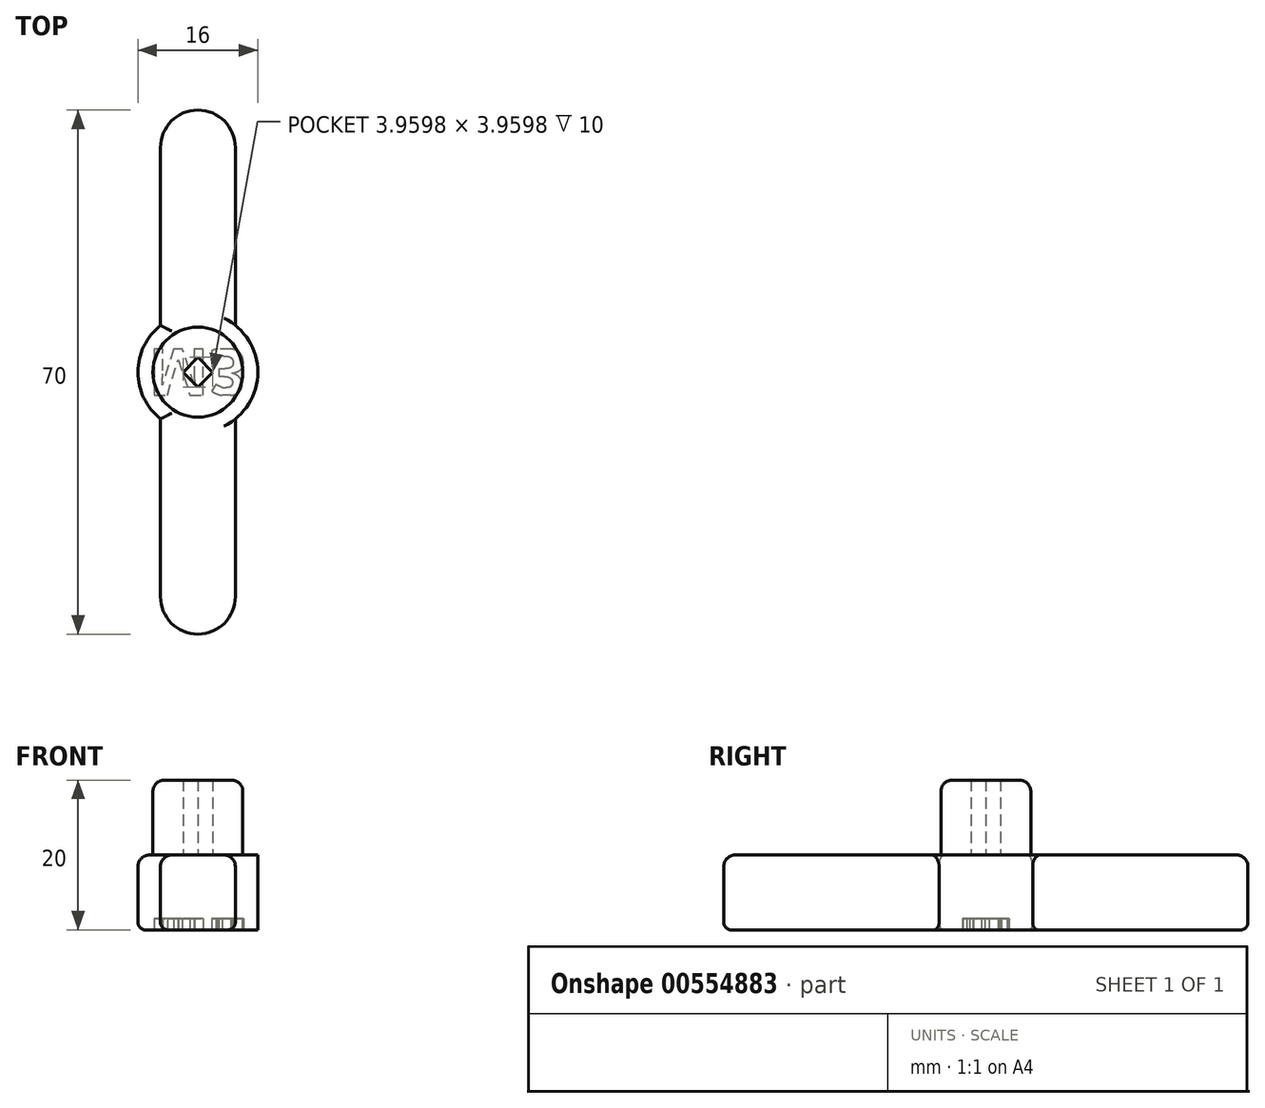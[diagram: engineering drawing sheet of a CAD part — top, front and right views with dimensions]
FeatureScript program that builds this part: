
annotation { "Feature Type Name" : "Feature", "Feature Type Description" : "" }
export const myFeature = defineFeature(function(context is Context, id is Id, definition is map)
    precondition{}
    {
        {
            var Q0;
            Q0=qCreatedBy(makeId("Top.planeOp"),FACE);
            var sketch = newSketch(context, id + "F0", { "sketchPlane" : qUnion([Q0])});
            skLineSegment(sketch, "E0.bottom", {"start": v(5, -30) * mm, "end": v(-5, -30) * mm});
            skLineSegment(sketch, "E0.top", {"start": v(5, 30) * mm, "end": v(-5, 30) * mm});
            skLineSegment(sketch, "E0.left", {"start": v(5, -30) * mm, "end": v(5, 30) * mm});
            skLineSegment(sketch, "E0.right", {"start": v(-5, -30) * mm, "end": v(-5, 30) * mm});
            skPoint(sketch, "E0.middle", {"position": v(0, 0) * mm});
            skArc(sketch, "E1", {"start": v(5, 30) * mm, "mid": v(0, 35) * mm, "end": v(-5, 30) * mm});
            skArc(sketch, "E2", {"start": v(-5, -30) * mm, "mid": v(0, -35) * mm, "end": v(5, -30) * mm});
            skCircle(sketch, "E3", {"center": v(0, 0) * mm, "radius": 8 * mm});
            skCircle(sketch, "E4", {"center": v(0, 0) * mm, "radius": 6 * mm});
            skCircle(sketch, "E5.cCircle", {"center": v(0, 0) * mm, "radius": 2.83 * mm, "construction": true});
            skLineSegment(sketch, "E5.0", {"start": v(0, -2.83) * mm, "end": v(-2.83, 0) * mm});
            skLineSegment(sketch, "E5.1", {"start": v(-2.83, 0) * mm, "end": v(0, 2.83) * mm});
            skLineSegment(sketch, "E5.2", {"start": v(0, 2.83) * mm, "end": v(2.83, 0) * mm});
            skLineSegment(sketch, "E5.3", {"start": v(2.83, 0) * mm, "end": v(0, -2.83) * mm});
            skSolve(sketch);
        }
        {
            var Q0;
            Q0=makeQuery(id+"F0.imprint","IMPRINT",FACE,{"disambiguationData":[TD([[makeQuery(id+"F0.imprint","IMPRINT",EDGE,{"derivedFrom":sQuery(id+"F0.wireOp",EDGE,"E5.0")}),1.0]])]});
            var Q1;
            {var subQ0=sQuery(id+"F0.wireOp",EDGE,"E4");var subQ1=sQuery(id+"F0.wireOp",EDGE,"E0.left");var subQ2=makeQuery(id+"F0.imprint","INTERSECT",VERTEX,{"disambiguationData":[OD(0.0)],"derivedFrom":[subQ1,subQ0]});Q1=makeQuery(id+"F0.imprint","IMPRINT",FACE,{"disambiguationData":[TD([[makeQuery(id+"F0.imprint","IMPRINT",EDGE,{"disambiguationData":[TD([[subQ2,-1.0]])],"derivedFrom":subQ1}),-1.0]])]});}
            var Q2;
            {var subQ0=sQuery(id+"F0.wireOp",EDGE,"E4");var subQ1=sQuery(id+"F0.wireOp",EDGE,"E0.right");var subQ2=makeQuery(id+"F0.imprint","INTERSECT",VERTEX,{"disambiguationData":[OD(0.0)],"derivedFrom":[subQ1,subQ0]});Q2=makeQuery(id+"F0.imprint","IMPRINT",FACE,{"disambiguationData":[TD([[makeQuery(id+"F0.imprint","IMPRINT",EDGE,{"disambiguationData":[TD([[subQ2,-1.0]])],"derivedFrom":subQ1}),1.0]])]});}
            extrude(context, id + "F1", {"entities" : qUnion([Q0, Q1, Q2]), "depth" : 20 * mm, "offsetDistance" : 25 * mm});
        }
        {
            var Q0;
            Q0 = qSketchRegion(id + "F0", true);
            extrude(context, id + "F2", {"entities" : qUnion([Q0]), "operationType" : NewBodyOperationType.ADD, "depth" : 10 * mm, "offsetDistance" : 25 * mm});
        }
        {
            var Q0;
            Q0=qCreatedBy(makeId("Top.planeOp"),FACE);
            var sketch = newSketch(context, id + "F3", { "sketchPlane" : qUnion([Q0])});
            skCircle(sketch, "E6", {"center": v(0, 0) * mm, "radius": 3.52 * mm});
            skSolve(sketch);
        }
        {
            var Q0;
            Q0=makeQuery(id+"F3.imprint","IMPRINT",FACE,{"disambiguationData":[TD([[makeQuery(id+"F3.imprint","IMPRINT",EDGE,{"derivedFrom":sQuery(id+"F3.wireOp",EDGE,"E6")}),1.0]])]});
            extrude(context, id + "F4", {"entities" : qUnion([Q0]), "operationType" : NewBodyOperationType.ADD, "depth" : 10 * mm, "offsetDistance" : 25 * mm});
        }
        {
            var Q0;
            {var subQ0=sQuery(id+"F0.wireOp",EDGE,"E4");Q0=makeQuery(id+"F4.boolean.opBoolean","MERGE",FACE,{"derivedFrom":[makeQuery(id+"F2.boolean.opBoolean","MERGE",FACE,{"derivedFrom":[makeQuery(id+"F1.opExtrude","CAP_FACE",FACE,{"disambiguationData":[OSD([subQ0,sQuery(id+"F0.wireOp",EDGE,"E5.0"),sQuery(id+"F0.wireOp",EDGE,"E5.1"),sQuery(id+"F0.wireOp",EDGE,"E5.2"),sQuery(id+"F0.wireOp",EDGE,"E5.3")])],"isStart":true}),makeQuery(id+"F2.opExtrude","CAP_FACE",FACE,{"disambiguationData":[OSD([sQuery(id+"F0.wireOp",EDGE,"E0.left"),sQuery(id+"F0.wireOp",EDGE,"E0.right"),sQuery(id+"F0.wireOp",EDGE,"E1"),sQuery(id+"F0.wireOp",EDGE,"E2"),sQuery(id+"F0.wireOp",EDGE,"E3"),subQ0])],"isStart":true})]}),makeQuery(id+"F4.opExtrude","CAP_FACE",FACE,{"disambiguationData":[OSD([sQuery(id+"F3.wireOp",EDGE,"E6")])],"isStart":true})]});}
            var sketch = newSketch(context, id + "F5", { "sketchPlane" : qUnion([Q0])});
            skLineSegment(sketch, "E7.bottom", {"start": v(6.64, -3.1) * mm, "end": v(-6.64, -3.1) * mm});
            skLineSegment(sketch, "E7.top", {"start": v(6.64, 3.1) * mm, "end": v(-6.64, 3.1) * mm});
            skLineSegment(sketch, "E7.left", {"start": v(6.64, -3.1) * mm, "end": v(6.64, 3.1) * mm});
            skLineSegment(sketch, "E7.right", {"start": v(-6.64, -3.1) * mm, "end": v(-6.64, 3.1) * mm});
            skPoint(sketch, "E7.middle", {"position": v(0, 0) * mm});
            skText(sketch, "E8", { "text": "M3\n", "fontName": "OpenSans-Bold.ttf"});
            const initialGuessF5  = {"E8": [-0.00664, -0.0031, 1, 0, 0.00621]};
            skSetInitialGuess(sketch, initialGuessF5);
            skSolve(sketch);
        }
        {
            var Q0;
            Q0=makeQuery(id+"F5.imprint","IMPRINT",FACE,{"disambiguationData":[TD([[makeQuery(id+"F5.imprint","IMPRINT",EDGE,{"derivedFrom":sQuery(id+"F5.wireOp",EDGE,"E8.sketch_text.stroke-19")}),-1.0]])]});
            var Q1;
            Q1=makeQuery(id+"F5.imprint","IMPRINT",FACE,{"disambiguationData":[TD([[makeQuery(id+"F5.imprint","IMPRINT",EDGE,{"derivedFrom":sQuery(id+"F5.wireOp",EDGE,"E8.sketch_text.stroke-0")}),-1.0]])]});
            extrude(context, id + "F6", {"entities" : qUnion([Q0, Q1]), "operationType" : NewBodyOperationType.REMOVE, "oppositeDirection" : true, "depth" : 1.5 * mm, "offsetDistance" : 25 * mm});
        }
        {
            var Q0;
            Q0=makeQuery(id+"F1.opExtrude","CAP_EDGE",EDGE,{"disambiguationData":[OSD([sQuery(id+"F0.wireOp",EDGE,"E4")])],"isStart":false});
            fillet(context, id + "F7", {"entities" : qUnion([Q0]), "radius" : 1.5 * mm, "tangentPropagation" : true, "allowEdgeOverflow" : false});
        }
        {
            var Q0;
            Q0=makeQuery(id+"F2.opExtrude","CAP_EDGE",EDGE,{"disambiguationData":[OSD([sQuery(id+"F0.wireOp",EDGE,"E2")])],"isStart":false});
            var Q1;
            {var subQ0=sQuery(id+"F0.wireOp",EDGE,"E0.right");Q1=makeQuery(id+"F2.opExtrude","CAP_EDGE",EDGE,{"disambiguationData":[OSD([subQ0]),TDD([makeQuery(id+"F0.imprint","IMPRINT",EDGE,{"disambiguationData":[TD([[makeQuery(id+"F0.imprint","INTERSECT",VERTEX,{"disambiguationData":[OD(0.0)],"derivedFrom":[subQ0,sQuery(id+"F0.wireOp",EDGE,"E3")]}),1.0]])],"derivedFrom":subQ0})])],"isStart":false});}
            var Q2;
            {var subQ0=sQuery(id+"F0.wireOp",EDGE,"E3");var subQ1=sQuery(id+"F0.wireOp",EDGE,"E0.right");Q2=makeQuery(id+"F2.opExtrude","CAP_EDGE",EDGE,{"disambiguationData":[OSD([subQ0]),TDD([makeQuery(id+"F0.imprint","IMPRINT",EDGE,{"disambiguationData":[TD([[makeQuery(id+"F0.imprint","INTERSECT",VERTEX,{"disambiguationData":[OD(0.0)],"derivedFrom":[subQ1,subQ0]}),1.0]])],"derivedFrom":subQ0})])],"isStart":false});}
            var Q3;
            {var subQ0=sQuery(id+"F0.wireOp",EDGE,"E0.right");Q3=makeQuery(id+"F2.opExtrude","CAP_EDGE",EDGE,{"disambiguationData":[OSD([subQ0]),TDD([makeQuery(id+"F0.imprint","IMPRINT",EDGE,{"disambiguationData":[TD([[makeQuery(id+"F0.imprint","INTERSECT",VERTEX,{"disambiguationData":[OD(1.0)],"derivedFrom":[subQ0,sQuery(id+"F0.wireOp",EDGE,"E3")]}),-1.0]])],"derivedFrom":subQ0})])],"isStart":false});}
            var Q4;
            Q4=makeQuery(id+"F2.opExtrude","CAP_EDGE",EDGE,{"disambiguationData":[OSD([sQuery(id+"F0.wireOp",EDGE,"E1")])],"isStart":false});
            var Q5;
            {var subQ0=sQuery(id+"F0.wireOp",EDGE,"E0.left");Q5=makeQuery(id+"F2.opExtrude","CAP_EDGE",EDGE,{"disambiguationData":[OSD([subQ0]),TDD([makeQuery(id+"F0.imprint","IMPRINT",EDGE,{"disambiguationData":[TD([[makeQuery(id+"F0.imprint","INTERSECT",VERTEX,{"disambiguationData":[OD(1.0)],"derivedFrom":[subQ0,sQuery(id+"F0.wireOp",EDGE,"E3")]}),-1.0]])],"derivedFrom":subQ0})])],"isStart":false});}
            var Q6;
            {var subQ0=sQuery(id+"F0.wireOp",EDGE,"E3");var subQ1=sQuery(id+"F0.wireOp",EDGE,"E0.left");Q6=makeQuery(id+"F2.opExtrude","CAP_EDGE",EDGE,{"disambiguationData":[OSD([subQ0]),TDD([makeQuery(id+"F0.imprint","IMPRINT",EDGE,{"disambiguationData":[TD([[makeQuery(id+"F0.imprint","INTERSECT",VERTEX,{"disambiguationData":[OD(0.0)],"derivedFrom":[subQ1,subQ0]}),-1.0]])],"derivedFrom":subQ0})])],"isStart":false});}
            var Q7;
            {var subQ0=sQuery(id+"F0.wireOp",EDGE,"E0.left");Q7=makeQuery(id+"F2.opExtrude","CAP_EDGE",EDGE,{"disambiguationData":[OSD([subQ0]),TDD([makeQuery(id+"F0.imprint","IMPRINT",EDGE,{"disambiguationData":[TD([[makeQuery(id+"F0.imprint","INTERSECT",VERTEX,{"disambiguationData":[OD(0.0)],"derivedFrom":[subQ0,sQuery(id+"F0.wireOp",EDGE,"E3")]}),1.0]])],"derivedFrom":subQ0})])],"isStart":false});}
            fillet(context, id + "F8", {"entities" : qUnion([Q0, Q1, Q2, Q3, Q4, Q5, Q6, Q7]), "radius" : 1.5 * mm, "tangentPropagation" : true, "allowEdgeOverflow" : false});
        }
        {
            var Q0;
            {var subQ0=sQuery(id+"F0.wireOp",EDGE,"E0.left");Q0=makeQuery(id+"F2.opExtrude","CAP_EDGE",EDGE,{"disambiguationData":[OSD([subQ0]),TDD([makeQuery(id+"F0.imprint","IMPRINT",EDGE,{"disambiguationData":[TD([[makeQuery(id+"F0.imprint","INTERSECT",VERTEX,{"disambiguationData":[OD(0.0)],"derivedFrom":[subQ0,sQuery(id+"F0.wireOp",EDGE,"E3")]}),1.0]])],"derivedFrom":subQ0})])],"isStart":true});}
            var Q1;
            Q1=makeQuery(id+"F2.opExtrude","CAP_EDGE",EDGE,{"disambiguationData":[OSD([sQuery(id+"F0.wireOp",EDGE,"E2")])],"isStart":true});
            var Q2;
            {var subQ0=sQuery(id+"F0.wireOp",EDGE,"E3");var subQ1=sQuery(id+"F0.wireOp",EDGE,"E0.right");Q2=makeQuery(id+"F2.opExtrude","CAP_EDGE",EDGE,{"disambiguationData":[OSD([subQ0]),TDD([makeQuery(id+"F0.imprint","IMPRINT",EDGE,{"disambiguationData":[TD([[makeQuery(id+"F0.imprint","INTERSECT",VERTEX,{"disambiguationData":[OD(0.0)],"derivedFrom":[subQ1,subQ0]}),1.0]])],"derivedFrom":subQ0})])],"isStart":true});}
            var Q3;
            {var subQ0=sQuery(id+"F0.wireOp",EDGE,"E0.right");Q3=makeQuery(id+"F2.opExtrude","CAP_EDGE",EDGE,{"disambiguationData":[OSD([subQ0]),TDD([makeQuery(id+"F0.imprint","IMPRINT",EDGE,{"disambiguationData":[TD([[makeQuery(id+"F0.imprint","INTERSECT",VERTEX,{"disambiguationData":[OD(0.0)],"derivedFrom":[subQ0,sQuery(id+"F0.wireOp",EDGE,"E3")]}),1.0]])],"derivedFrom":subQ0})])],"isStart":true});}
            var Q4;
            {var subQ0=sQuery(id+"F0.wireOp",EDGE,"E0.left");Q4=makeQuery(id+"F2.opExtrude","CAP_EDGE",EDGE,{"disambiguationData":[OSD([subQ0]),TDD([makeQuery(id+"F0.imprint","IMPRINT",EDGE,{"disambiguationData":[TD([[makeQuery(id+"F0.imprint","INTERSECT",VERTEX,{"disambiguationData":[OD(1.0)],"derivedFrom":[subQ0,sQuery(id+"F0.wireOp",EDGE,"E3")]}),-1.0]])],"derivedFrom":subQ0})])],"isStart":true});}
            var Q5;
            {var subQ0=sQuery(id+"F0.wireOp",EDGE,"E0.right");Q5=makeQuery(id+"F2.opExtrude","CAP_EDGE",EDGE,{"disambiguationData":[OSD([subQ0]),TDD([makeQuery(id+"F0.imprint","IMPRINT",EDGE,{"disambiguationData":[TD([[makeQuery(id+"F0.imprint","INTERSECT",VERTEX,{"disambiguationData":[OD(1.0)],"derivedFrom":[subQ0,sQuery(id+"F0.wireOp",EDGE,"E3")]}),-1.0]])],"derivedFrom":subQ0})])],"isStart":true});}
            var Q6;
            Q6=makeQuery(id+"F2.opExtrude","CAP_EDGE",EDGE,{"disambiguationData":[OSD([sQuery(id+"F0.wireOp",EDGE,"E1")])],"isStart":true});
            var Q7;
            {var subQ0=sQuery(id+"F0.wireOp",EDGE,"E3");var subQ1=sQuery(id+"F0.wireOp",EDGE,"E0.left");Q7=makeQuery(id+"F2.opExtrude","CAP_EDGE",EDGE,{"disambiguationData":[OSD([subQ0]),TDD([makeQuery(id+"F0.imprint","IMPRINT",EDGE,{"disambiguationData":[TD([[makeQuery(id+"F0.imprint","INTERSECT",VERTEX,{"disambiguationData":[OD(0.0)],"derivedFrom":[subQ1,subQ0]}),-1.0]])],"derivedFrom":subQ0})])],"isStart":true});}
            fillet(context, id + "F9", {"entities" : qUnion([Q0, Q1, Q2, Q3, Q4, Q5, Q6, Q7]), "radius" : 1 * mm, "tangentPropagation" : true, "allowEdgeOverflow" : false});
        }
        {
            var Q0;
            Q0=makeQuery(id+"F4.opExtrude","CAP_FACE",FACE,{"disambiguationData":[OSD([sQuery(id+"F3.wireOp",EDGE,"E6")])],"isStart":false});
            var sketch = newSketch(context, id + "F10", { "sketchPlane" : qUnion([Q0])});
            skCircle(sketch, "E9.cCircle", {"center": v(0, 0) * mm, "radius": 1.98 * mm, "construction": true});
            skLineSegment(sketch, "E9.0", {"start": v(0, 1.98) * mm, "end": v(1.98, 0) * mm});
            skLineSegment(sketch, "E9.1", {"start": v(1.98, 0) * mm, "end": v(0, -1.98) * mm});
            skLineSegment(sketch, "E9.2", {"start": v(0, -1.98) * mm, "end": v(-1.98, 0) * mm});
            skLineSegment(sketch, "E9.3", {"start": v(-1.98, 0) * mm, "end": v(0, 1.98) * mm});
            skSolve(sketch);
        }
        {
            var Q0;
            Q0=makeQuery(id+"F10.imprint","IMPRINT",FACE,{"disambiguationData":[TD([[makeQuery(id+"F10.imprint","IMPRINT",EDGE,{"derivedFrom":sQuery(id+"F10.wireOp",EDGE,"E9.0")}),1.0]])]});
            extrude(context, id + "F11", {"entities" : qUnion([Q0]), "operationType" : NewBodyOperationType.ADD, "depth" : 10 * mm, "offsetDistance" : 25 * mm});
        }
    });
